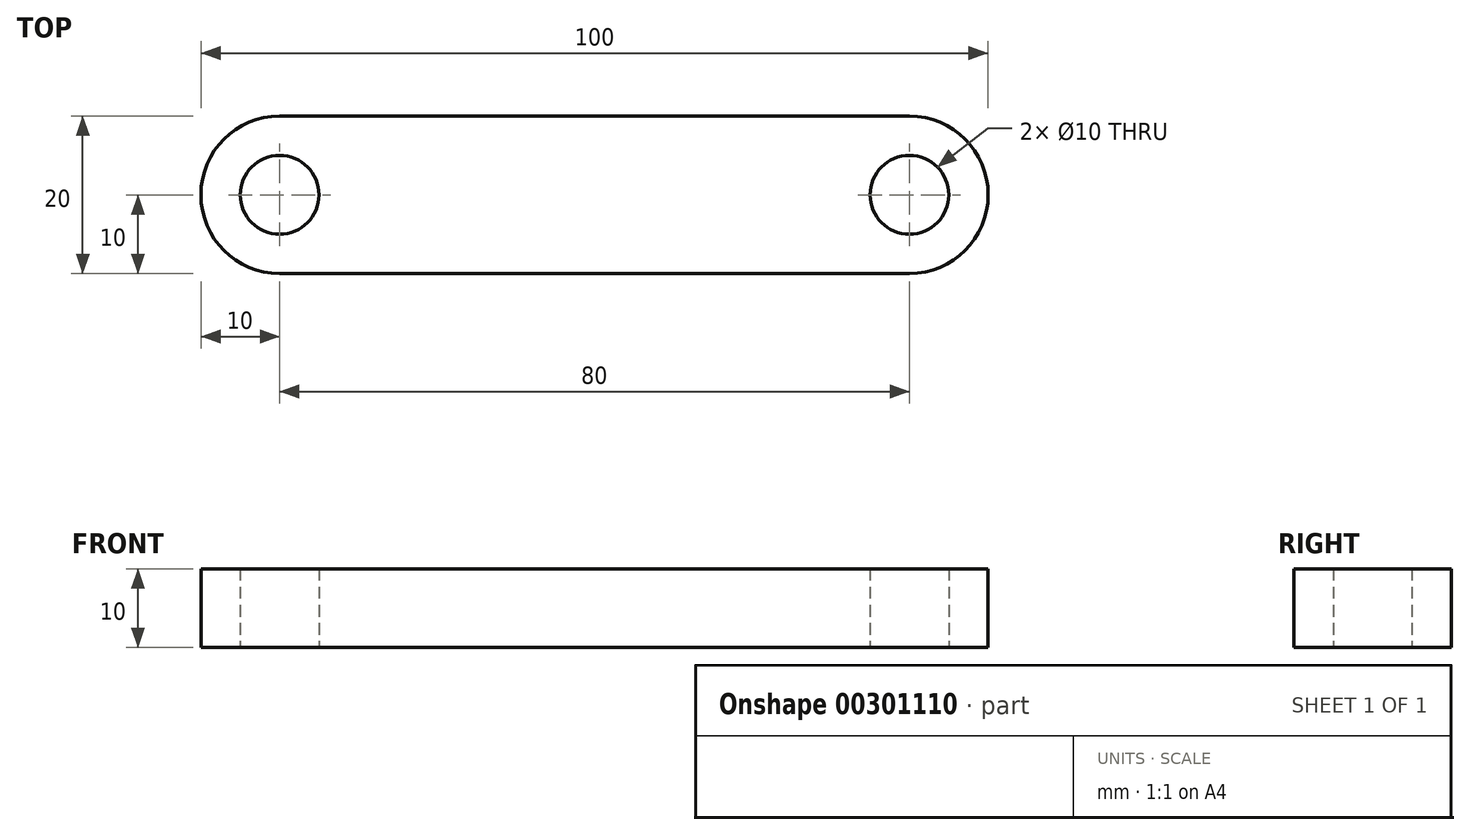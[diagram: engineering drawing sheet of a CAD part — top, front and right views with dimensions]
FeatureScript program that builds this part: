
annotation { "Feature Type Name" : "Feature", "Feature Type Description" : "" }
export const myFeature = defineFeature(function(context is Context, id is Id, definition is map)
    precondition{}
    {
        {
            var Q0;
            Q0=qCreatedBy(makeId("Top.planeOp"),FACE);
            var sketch = newSketch(context, id + "F0", { "sketchPlane" : qUnion([Q0])});
            skLineSegment(sketch, "E0", {"start": v(0, 0) * mm, "end": v(80, 0) * mm});
            skLineSegment(sketch, "E1", {"start": v(0, 20) * mm, "end": v(80, 20) * mm});
            skArc(sketch, "E2", {"start": v(0, 20) * mm, "mid": v(-10, 10) * mm, "end": v(0, 0) * mm});
            skArc(sketch, "E3", {"start": v(80, 0) * mm, "mid": v(90, 10) * mm, "end": v(80, 20) * mm});
            skSolve(sketch);
        }
        {
            var Q0;
            Q0 = qSketchRegion(id + "F0", true);
            extrude(context, id + "F1", {"entities" : qUnion([Q0]), "depth" : 10 * mm});
        }
        {
            var Q0;
            Q0=qCreatedBy(makeId("Top.planeOp"),FACE);
            var sketch = newSketch(context, id + "F2", { "sketchPlane" : qUnion([Q0])});
            skCircle(sketch, "E4", {"center": v(0, 10) * mm, "radius": 5 * mm});
            skCircle(sketch, "E5", {"center": v(80, 10) * mm, "radius": 5 * mm});
            skSolve(sketch);
        }
        {
            var Q0;
            Q0 = qSketchRegion(id + "F2", true);
            extrude(context, id + "F3", {"entities" : qUnion([Q0]), "operationType" : NewBodyOperationType.REMOVE, "depth" : 25 * mm});
        }
    });
